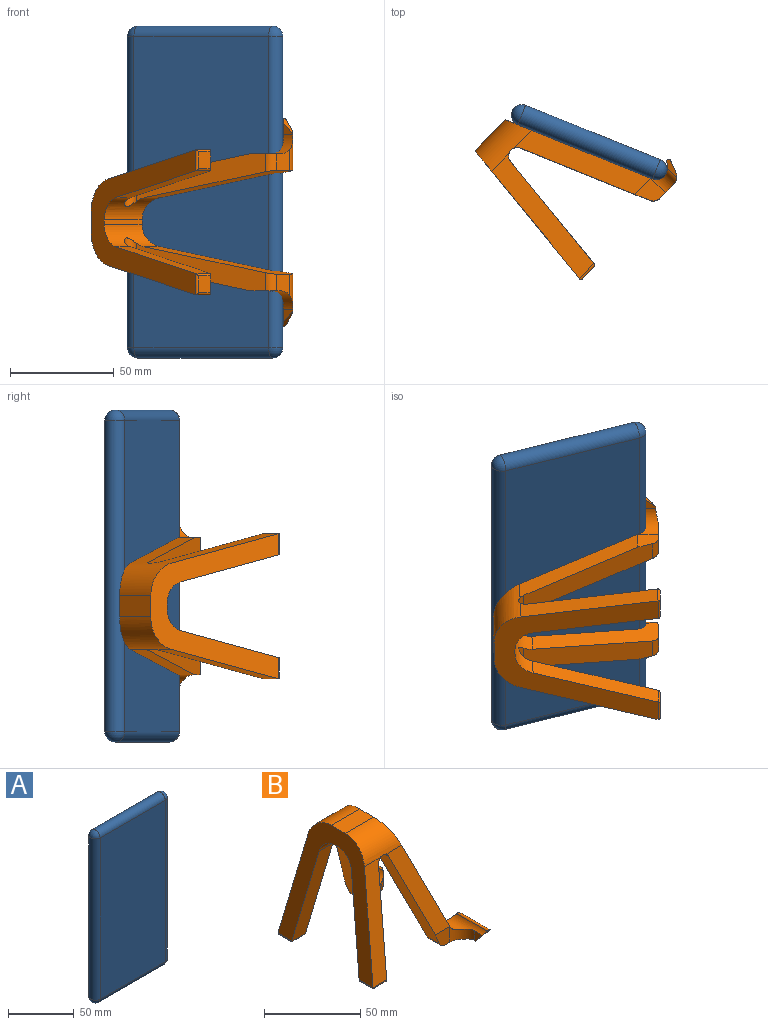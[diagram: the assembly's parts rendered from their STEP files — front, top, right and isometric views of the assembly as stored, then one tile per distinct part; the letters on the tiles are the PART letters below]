
ASSEMBLY  parts=2 mates=1
PART A: 10 faces, bbox 80x10x160 mm
  f0: plane 150x70mm, normal (0,-1,0), area 10500mm2, adj f3,f4,f7,f8
  f1: plane 150x70mm, normal (0,1,0), area 10500mm2, adj f3,f4,f7,f8
  f2: sphere r=5mm, area 78.5mm2, adj f3,f4
  f3: cylinder r=5mm len=70mm, axis (1,0,0), area 1099.6mm2, adj f0,f1,f2,f5
  f4: cylinder r=5mm len=150mm, axis (0,0,-1), area 2356.2mm2, adj f0,f1,f2,f6
  f5: sphere r=5mm, area 78.5mm2, adj f3,f7
  f6: sphere r=5mm, area 78.5mm2, adj f4,f8
  f7: cylinder r=5mm len=150mm, axis (0,0,1), area 2356.2mm2, adj f0,f1,f5,f9
  f8: cylinder r=5mm len=70mm, axis (-1,0,0), area 1099.6mm2, adj f0,f1,f6,f9
  f9: sphere r=5mm, area 78.5mm2, adj f7,f8
PART B: 58 faces, bbox 71.7x100.2x80.2 mm
  f0: plane 1.26x0.22mm, normal (0,1,0), area 0.2mm2, adj f4,f45
  f1: cylinder r=6mm len=26.81mm, axis (0,-1,0), area 191.7mm2, adj f4,f5,f12,f23,f36,f43,f45
  f2: plane 10.25x9.22mm, normal (0,0,-1), area 78.5mm2, adj f23,f35,f36,f56,f57
  f3: plane 22.76x6.02mm, normal (0.93,0,-0.37), area 119.9mm2, adj f4,f43,f45,f56
  f4: cylinder r=1mm len=22.93mm, axis (0,-1,0), area 61mm2, adj f0,f1,f3,f42,f43,f45
  f5: plane 6.21x5.72mm, normal (-1,0,0), area 20.4mm2, adj f1,f36,f45,f56
  f6: plane 1.26x0.22mm, normal (0,-1,0), area 0.2mm2, adj f10,f44
  f7: plane 10.25x9.22mm, normal (0,0,-1), area 78.5mm2, adj f13,f38,f39,f54,f55
  f8: plane 62.32x25.22mm, normal (-0.93,0,-0.37), area 682.4mm2, adj f13,f14,f19,f27,f39,f54
  f9: plane 22.76x6.02mm, normal (0.93,0,-0.37), area 119.9mm2, adj f10,f40,f44,f55
  f10: cylinder r=1mm len=22.93mm, axis (0,-1,0), area 61mm2, adj f6,f9,f11,f40,f41,f44
  f11: cylinder r=6mm len=26.81mm, axis (0,-1,0), area 191.7mm2, adj f10,f12,f13,f37,f38,f40,f44
  f12: plane 70x66.15mm, normal (0.93,0,0.37), area 1699.4mm2, adj f1,f11,f13,f14,f23,f25,f26,f27
  f13: plane 61.5x40.17mm, normal (0,0.98,-0.21), area 705mm2, adj f7,f8,f11,f12,f27,f40,f54,f55
  f14: plane 57.37x34.9mm, normal (0,-0.98,0.21), area 632.7mm2, adj f8,f12,f19,f30,f39
  f15: plane 8.18x8.06mm, normal (0,0,-1), area 65.9mm2, adj f46,f47,f48,f49
  f16: plane 8.18x8.06mm, normal (0,0,-1), area 65.9mm2, adj f50,f51,f52,f53
  f17: plane 62.32x25.22mm, normal (-0.93,0,-0.37), area 682.4mm2, adj f18,f23,f25,f33,f35,f57
  f18: cylinder r=4.07mm len=13.9mm, axis (0,-1,0), area 131mm2, adj f17,f20,f25,f32,f33,f34
  f19: cylinder r=4.07mm len=13.9mm, axis (0,-1,0), area 131mm2, adj f8,f14,f21,f27,f29,f30
  f20: plane 63.46x24.27mm, normal (0.99,0,-0.12), area 653.9mm2, adj f18,f24,f25,f34,f47,f49
  f21: plane 63.46x24.27mm, normal (0.99,0,-0.12), area 653.9mm2, adj f19,f27,f28,f29,f51,f53
  f22: plane 78.88x69.97mm, normal (-0.99,0,0.12), area 1769.6mm2, adj f24,f25,f26,f27,f28,f29,f30,f31
  f23: plane 61.5x40.17mm, normal (0,-0.98,-0.21), area 705mm2, adj f1,f2,f12,f17,f25,f43,f56,f57
  f24: plane 60.51x17.21mm, normal (0,-0.98,-0.21), area 623.2mm2, adj f20,f22,f25,f46,f47,f48
  f25: cylinder r=11mm len=30.67mm, axis (-1,0,0), area 356.7mm2, adj f12,f17,f18,f20,f22,f23,f24,f26
  f26: plane 26.13x2.22mm, normal (0,0,-1), area 57.9mm2, adj f12,f22,f25,f27
  f27: cylinder r=11mm len=30.67mm, axis (-1,0,0), area 356.7mm2, adj f8,f12,f13,f19,f21,f22,f26,f28
  f28: plane 60.51x17.21mm, normal (0,0.98,-0.21), area 623.2mm2, adj f21,f22,f27,f50,f51,f52
  f29: plane 66.24x19.62mm, normal (0,-0.98,0.21), area 682.6mm2, adj f19,f21,f22,f30,f53
  f30: cylinder r=16mm len=27.51mm, axis (-1,0,0), area 504.2mm2, adj f12,f14,f19,f22,f29,f31
  f31: plane 20.9x10.3mm, normal (0,0,1), area 215.3mm2, adj f12,f22,f30,f32
  f32: cylinder r=16mm len=27.51mm, axis (-1,0,0), area 504.2mm2, adj f12,f18,f22,f31,f33,f34
  f33: plane 57.37x34.9mm, normal (0,0.98,0.21), area 632.7mm2, adj f12,f17,f18,f32,f35
  f34: plane 66.24x19.62mm, normal (0,0.98,0.21), area 682.6mm2, adj f18,f20,f22,f32,f49
  f35: plane 10.79x10.04mm, normal (0,1,0), area 85.9mm2, adj f2,f17,f33,f36,f57
  f36: cylinder r=9mm len=10.04mm, axis (0,0,-1), area 94.3mm2, adj f1,f2,f5,f12,f35,f56
  f37: plane 6.21x5.72mm, normal (-1,0,0), area 20.4mm2, adj f11,f38,f44,f55
  f38: cylinder r=9mm len=10.04mm, axis (0,0,-1), area 94.3mm2, adj f7,f11,f12,f37,f39,f55
  f39: plane 10.79x10.04mm, normal (0,-1,0), area 85.9mm2, adj f7,f8,f14,f38,f54
  f40: cylinder r=9mm len=9.63mm, axis (0,0,-1), area 44.3mm2, adj f9,f10,f11,f13,f41,f55
  f41: plane 0.45x0.03mm, normal (0,1,0), area 0mm2, adj f10,f40
  f42: plane 0.45x0.03mm, normal (0,-1,0), area 0mm2, adj f4,f43
  f43: cylinder r=9mm len=9.63mm, axis (0,0,-1), area 44.3mm2, adj f1,f3,f4,f23,f42,f56
  f44: plane 9.25x7.27mm, normal (0,-0.79,-0.62), area 23.1mm2, adj f6,f9,f10,f11,f37,f55
  f45: plane 9.25x7.27mm, normal (0,0.79,-0.62), area 23.1mm2, adj f0,f1,f3,f4,f5,f56
  f46: cylinder r=1mm len=10.01mm, axis (1,0,0), area 12.5mm2, adj f15,f24,f47,f48
  f47: cylinder r=1mm len=10.17mm, axis (0,-1,0), area 13.7mm2, adj f15,f20,f24,f46,f49
  f48: cylinder r=1mm len=10.23mm, axis (0,1,0), area 16.1mm2, adj f15,f22,f24,f46,f49
  f49: cylinder r=1mm len=10.09mm, axis (-1,0,0), area 16.8mm2, adj f15,f20,f22,f34,f47,f48
  f50: cylinder r=1mm len=10.01mm, axis (1,0,0), area 12.5mm2, adj f16,f28,f51,f52
  f51: cylinder r=1mm len=10.17mm, axis (0,-1,0), area 13.7mm2, adj f16,f21,f28,f50,f53
  f52: cylinder r=1mm len=10.23mm, axis (0,1,0), area 16.1mm2, adj f16,f22,f28,f50,f53
  f53: cylinder r=1mm len=10.09mm, axis (-1,0,0), area 16.8mm2, adj f16,f21,f22,f29,f51,f52
  f54: cylinder r=5mm len=8.75mm, axis (0,-1,0), area 49.3mm2, adj f7,f8,f13,f39
  f55: cylinder r=5mm len=19.68mm, axis (0,1,0), area 88mm2, adj f7,f9,f13,f37,f38,f40,f44
  f56: cylinder r=5mm len=19.68mm, axis (0,1,0), area 88mm2, adj f2,f3,f5,f23,f36,f43,f45
  f57: cylinder r=5mm len=8.75mm, axis (0,-1,0), area 49.3mm2, adj f2,f17,f23,f35
PLACE A rot(axis=(0,0,-1),22deg) t=(-106.88,-1.19,-44.75)mm
PLACE B rot(axis=(-0.86,-0.36,0.36),98.8deg) t=(-75.62,-87.31,20.67)mm
MATE planar B.f12 <-> A.f0  axis (0.37,0.93,0) through (-79.54,-23.01,20.67)mm
